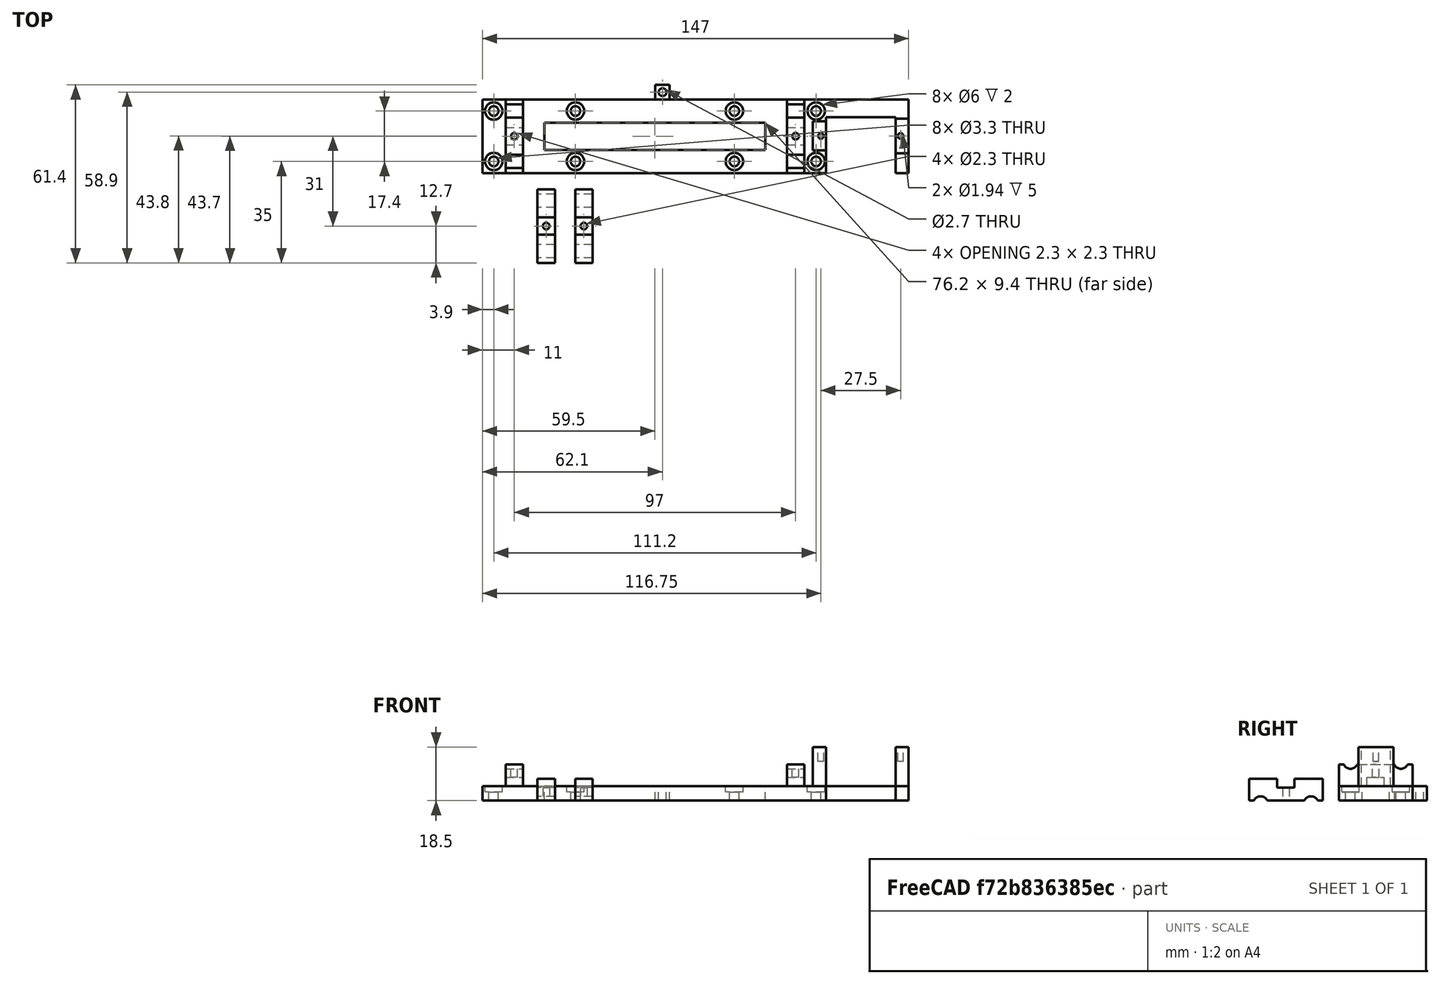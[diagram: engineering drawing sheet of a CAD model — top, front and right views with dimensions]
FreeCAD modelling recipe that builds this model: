
FCSTD DOCUMENT
Label: beam
objects: Part::Cut×23, Part::Cylinder×19, Part::Box×7, Part::MultiFuse×2
note: 51 computed .brp shape members not serialized (recipe doc carries the construction recipe); baked Part::Feature solids carry a one-line shape summary decoded from their .brp

FEATURE [Part::Box] Box
  Height = 5
  Length = 147
  Width = 25.4
FEATURE [Part::Box] Box001
  Height = 12.4
  Length = 76.2
  Placement = pos=(21.4,8,0) rot=(0,0,1;0rad)
  Width = 9.4
FEATURE [Part::Cut] Cut
  Base = -> Box
  Tool = -> Box001
FEATURE [Part::Cylinder] Cylinder
  Angle = 360
  Height = 10
  Placement = pos=(3.9,4,0) rot=(0,0,1;0rad)
  Radius = 1.65
FEATURE [Part::Cylinder] Cylinder001
  Angle = 360
  Height = 10
  Placement = pos=(3.9,21.4,0) rot=(0,0,1;0rad)
  Radius = 1.65
FEATURE [Part::Cylinder] Cylinder002
  Angle = 360
  Height = 10
  Placement = pos=(32.1,4,0) rot=(0,0,1;0rad)
  Radius = 1.65
FEATURE [Part::Cylinder] Cylinder002001
  Angle = 360
  Height = 10
  Placement = pos=(32.1,21.4,0) rot=(0,0,1;0rad)
  Radius = 1.65
FEATURE [Part::MultiFuse] Fusion
  Shapes = -> [Cylinder002001,Cylinder001,Cylinder,Cylinder002]
FEATURE [Part::MultiFuse] Fusion001
  Placement = pos=(83,0,0) rot=(0,0,1;0rad)
  Shapes = -> [Cylinder002001,Cylinder001,Cylinder,Cylinder002]
FEATURE [Part::Box] Box003
  Height = 10
  Length = 24
  Placement = pos=(118.5,0,0) rot=(0,0,1;0rad)
  Width = 19.2
FEATURE [Part::Cut] Cut001
  Base = -> Cut
  Tool = -> Fusion001
FEATURE [Part::Cut] Cut002
  Base = -> Cut001
  Tool = -> Fusion
FEATURE [Part::Cut] Cut003
  Base = -> Cut002
  Tool = -> Box003
FEATURE [Part::Box] Box005
  Height = 5
  Length = 5
  Placement = pos=(59.6,25.4,0) rot=(0,0,1;0rad)
  Width = 5
FEATURE [Part::Box] Box006
  Height = 13.5
  Length = 4.5
  Placement = pos=(142.5,6.8,5) rot=(0,0,1;0rad)
  Width = 12
FEATURE [Part::Box] Box006001
  Height = 13.5
  Length = 4.5
  Placement = pos=(114,7.8,5) rot=(0,0,1;0rad)
  Width = 10
FEATURE [Part::Cylinder] Cylinder002002
  Angle = 360
  Height = 2
  Placement = pos=(3.9,4,3) rot=(0,0,1;0rad)
  Radius = 3
FEATURE [Part::Cut] Cut013003003
  Base = -> Cut003
  Tool = -> Cylinder002002
FEATURE [Part::Cylinder] Cylinder002002001
  Angle = 360
  Height = 2
  Placement = pos=(3.9,21.4,3) rot=(0,0,1;0rad)
  Radius = 3
FEATURE [Part::Cylinder] Cylinder002002001001
  Angle = 360
  Height = 2
  Placement = pos=(32.1,21.4,3) rot=(0,0,1;0rad)
  Radius = 3
FEATURE [Part::Cylinder] Cylinder002002001001001
  Angle = 360
  Height = 2
  Placement = pos=(32.1,4,3) rot=(0,0,1;0rad)
  Radius = 3
FEATURE [Part::Cylinder] Cylinder002002001001001001
  Angle = 360
  Height = 2
  Placement = pos=(86.9,4,3) rot=(0,0,1;0rad)
  Radius = 3
FEATURE [Part::Cylinder] Cylinder002002001001001001001
  Angle = 360
  Height = 2
  Placement = pos=(86.9,21.4,3) rot=(0,0,1;0rad)
  Radius = 3
FEATURE [Part::Cylinder] Cylinder002002001001001001001001
  Angle = 360
  Height = 2
  Placement = pos=(115.1,21.4,3) rot=(0,0,1;0rad)
  Radius = 3
FEATURE [Part::Cylinder] Cylinder002002001001001001001001001
  Angle = 360
  Height = 2
  Placement = pos=(115.1,4,3) rot=(0,0,1;0rad)
  Radius = 3
FEATURE [Part::Cut] Cut013003004
  Base = -> Cut013003003
  Tool = -> Cylinder002002001
FEATURE [Part::Cut] Cut013003005
  Base = -> Cut013003004
  Tool = -> Cylinder002002001001001001001001001
FEATURE [Part::Cut] Cut013003006
  Base = -> Cut013003005
  Tool = -> Cylinder002002001001001001001001
FEATURE [Part::Cut] Cut013003007
  Base = -> Cut013003006
  Tool = -> Cylinder002002001001001001001
FEATURE [Part::Cut] Cut013003008
  Base = -> Cut013003007
  Tool = -> Cylinder002002001001001001
FEATURE [Part::Cut] Cut013003009
  Base = -> Cut013003008
  Tool = -> Cylinder002002001001001
FEATURE [Part::Cut] Cut013003010
  Base = -> Cut013003009
  Tool = -> Cylinder002002001001
FEATURE [Part::Cylinder] Cylinder002002001001001001001001002
  Angle = 360
  Height = 111
  Placement = pos=(4,4,13.5) rot=(0,1,0;1.5708rad)
  Radius = 2.5
FEATURE [Part::Cylinder] Cylinder002002001001001001001001003
  Angle = 360
  Height = 111
  Placement = pos=(4,21.4,13.5) rot=(0,1,0;1.5708rad)
  Radius = 2.5
FEATURE [Part::Box] Box006004
  Height = 3
  Length = 6
  Placement = pos=(8,9.7,5) rot=(0,0,1;0rad)
  Width = 6
FEATURE [Part::Cut] Cut013003012
FEATURE [Part::Cut] Cut013003013
  Placement = pos=(97,0,0) rot=(0,0,1;0rad)
FEATURE [Part::Cylinder] Cylinder002002001001001001001001004
  Angle = 360
  Height = 111
  Placement = pos=(4,4,13.5) rot=(0,1,0;1.5708rad)
  Radius = 2.5
FEATURE [Part::Cylinder] Cylinder002002001001001001001001005
  Angle = 360
  Height = 111
  Placement = pos=(4,21.4,13.5) rot=(0,1,0;1.5708rad)
  Radius = 2.5
FEATURE [Part::Cut] Cut013003014
  Base = -> Cut013003012
  Tool = -> Cylinder002002001001001001001001002
FEATURE [Part::Cut] Cut013003015
  Base = -> Cut013003014
  Tool = -> Cylinder002002001001001001001001003
FEATURE [Part::Cut] Cut013003016
  Base = -> Cut013003013
  Tool = -> Cylinder002002001001001001001001004
FEATURE [Part::Cut] Cut013003017
  Base = -> Cut013003016
  Tool = -> Cylinder002002001001001001001001005
FEATURE [Part::Cut] Cut013003018
  Base = -> Cut013003014
  Placement = pos=(33,-31,12.5) rot=(0,1,0;3.14159rad)
  Tool = -> Cylinder002002001001001001001001003
FEATURE [Part::Cut] Cut013003019
  Base = -> Cut013003014
  Placement = pos=(46,-31,12.5) rot=(0,1,0;3.14159rad)
  Tool = -> Cylinder002002001001001001001001003
FEATURE [Part::Cylinder] Cylinder002002001001001001001001006
  Angle = 360
  Height = 5
  Placement = pos=(62.1,27.9,0) rot=(0,0,1;0rad)
  Radius = 1.35
FEATURE [Part::Cut] Cut013003020
  Base = -> Box005
  Tool = -> Cylinder002002001001001001001001006
FEATURE [Part::Cylinder] Cylinder002002001001001001001001007
  Angle = 360
  Height = 5
  Placement = pos=(116.75,12.8,13.5) rot=(0,0,1;0rad)
  Radius = 0.97
FEATURE [Part::Cylinder] Cylinder002002001001001001001001008
  Angle = 360
  Height = 5
  Placement = pos=(144.25,12.8,13.5) rot=(0,0,1;0rad)
  Radius = 0.97
FEATURE [Part::Cut] Cut013003021
  Base = -> Box006
  Tool = -> Cylinder002002001001001001001001008
FEATURE [Part::Cut] Cut013003022
  Base = -> Box006001
  Tool = -> Cylinder002002001001001001001001007
